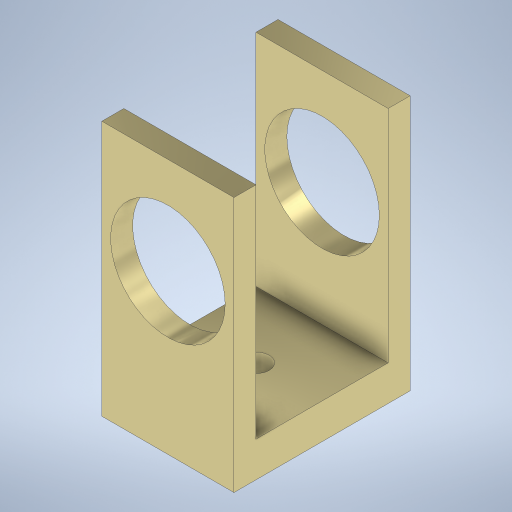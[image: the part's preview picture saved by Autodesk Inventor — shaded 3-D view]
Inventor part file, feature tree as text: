
AUTODESK INVENTOR PART (.ipt)
format: ipt  version: 2024 (Build 280153000, 153)  size: 279,040 bytes
history: native  units: mm
features: extrude x4, sketch x4
ambient origin geometry x8: Origin, YZ Plane, XZ Plane, XY Plane, X Axis, Y Axis, Z Axis, Center Point
bodies: Solid1 (feature_tree)
feature tree (8):
  extrude  "Extrusion1"  Depth=20.0mm
  extrude  "Extrusion2"  Depth=2.5mm
  extrude  "Extrusion4"  Depth=25.0mm
  extrude  "Extrusion5"  Depth=25.0mm
  sketch  "Sketch1"  dims[d0=15.0mm d1=20.0mm]
  sketch  "Sketch2"  dims[d2=4.0mm d3=0.0mm d4=2.5mm]
  sketch  "Sketch4"  dims[d5=25.0mm d6=0.0mm d12=7.0mm]
  sketch  "Sketch5"  dims[d13=13.0mm d14=5.984189mm d15=25.0mm d16=0.0mm d17=3.0mm d18=5.0mm d19=0.0mm d11=0.5mm]
